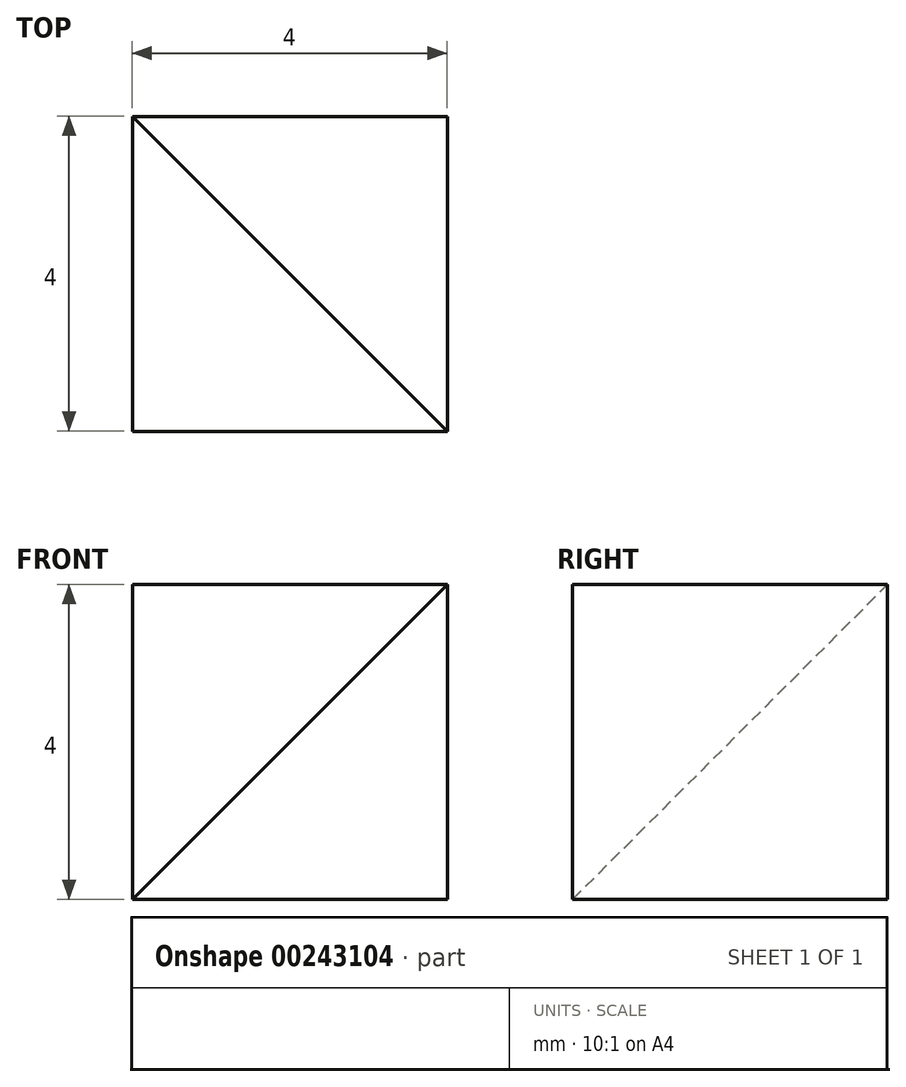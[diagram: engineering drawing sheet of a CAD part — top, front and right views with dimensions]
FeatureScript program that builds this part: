
annotation { "Feature Type Name" : "Feature", "Feature Type Description" : "" }
export const myFeature = defineFeature(function(context is Context, id is Id, definition is map)
    precondition{}
    {
        {
            var Q0;
            Q0=qCreatedBy(makeId("Top.planeOp"),FACE);
            var sketch = newSketch(context, id + "F0", { "sketchPlane" : qUnion([Q0])});
            skLineSegment(sketch, "E0.bottom", {"start": v(20.07, 23.16) * mm, "end": v(24.07, 23.16) * mm});
            skLineSegment(sketch, "E0.top", {"start": v(20.07, 19.16) * mm, "end": v(24.07, 19.16) * mm});
            skLineSegment(sketch, "E0.left", {"start": v(20.07, 23.16) * mm, "end": v(20.07, 19.16) * mm});
            skLineSegment(sketch, "E0.right", {"start": v(24.07, 23.16) * mm, "end": v(24.07, 19.16) * mm});
            skSolve(sketch);
        }
        {
            var Q0;
            Q0=makeQuery(id+"F0.imprint","IMPRINT",FACE,{"disambiguationData":[TD([[makeQuery(id+"F0.imprint","IMPRINT",EDGE,{"derivedFrom":sQuery(id+"F0.wireOp",EDGE,"E0.bottom")}),-1.0]])]});
            extrude(context, id + "F1", {"entities" : qUnion([Q0]), "depth" : 4 * mm});
        }
        {
            var Q0;
            Q0=makeQuery(id+"F1.opExtrude","CAP_VERTEX",VERTEX,{"disambiguationData":[OSD([sQuery(id+"F0.wireOp",EDGE,"E0.bottom"),sQuery(id+"F0.wireOp",EDGE,"E0.left")])],"isStart":false});
            var Q1;
            Q1=makeQuery(id+"F1.opExtrude","CAP_VERTEX",VERTEX,{"disambiguationData":[OSD([sQuery(id+"F0.wireOp",EDGE,"E0.top"),sQuery(id+"F0.wireOp",EDGE,"E0.right")])],"isStart":false});
            var Q2;
            Q2=makeQuery(id+"F1.opExtrude","CAP_VERTEX",VERTEX,{"disambiguationData":[OSD([sQuery(id+"F0.wireOp",EDGE,"E0.top"),sQuery(id+"F0.wireOp",EDGE,"E0.left")])],"isStart":true});
            cPlane(context, id + "F2", {"entities" : qUnion([Q0, Q1, Q2]), "cplaneType" : CPlaneType.THREE_POINT, "offset" : 25 * mm, "width" : 150 * mm, "height" : 150 * mm});
        }
        {
            var Q0;
            Q0=qCreatedBy(id+"F2.planeOp",FACE);
            var sketch = newSketch(context, id + "F3", { "sketchPlane" : qUnion([Q0])});
            skPoint(sketch, "E1.0", {"position": v(8.57, 19.2) * mm});
            skPoint(sketch, "E2.0", {"position": v(13.47, 16.37) * mm});
            skPoint(sketch, "E3.0", {"position": v(8.57, 13.55) * mm});
            skLineSegment(sketch, "E4", {"start": v(8.57, 19.2) * mm, "end": v(13.47, 16.37) * mm});
            skLineSegment(sketch, "E5", {"start": v(13.47, 16.37) * mm, "end": v(8.57, 13.55) * mm});
            skLineSegment(sketch, "E6", {"start": v(8.57, 13.55) * mm, "end": v(8.57, 19.2) * mm});
            skSolve(sketch);
        }
        {
            var Q0;
            Q0 = qSketchRegion(id + "F3", true);
            extrude(context, id + "F4", {"entities" : qUnion([Q0]), "operationType" : NewBodyOperationType.REMOVE, "depth" : 25 * mm});
        }
        {
            var Q0;
            Q0=makeQuery(id+"F1.opExtrude","CAP_VERTEX",VERTEX,{"disambiguationData":[OSD([sQuery(id+"F0.wireOp",EDGE,"E0.bottom"),sQuery(id+"F0.wireOp",EDGE,"E0.right")])],"isStart":true});
            var Q1;
            Q1=makeQuery(id+"F4.boolean.opBoolean","MERGE",VERTEX,{"derivedFrom":[makeQuery(id+"F1.opExtrude","CAP_VERTEX",VERTEX,{"disambiguationData":[OSD([sQuery(id+"F0.wireOp",EDGE,"E0.top"),sQuery(id+"F0.wireOp",EDGE,"E0.right")])],"isStart":false}),makeQuery(id+"F4.opExtrude","CAP_VERTEX",VERTEX,{"disambiguationData":[OSD([sQuery(id+"F3.wireOp",EDGE,"E4"),sQuery(id+"F3.wireOp",EDGE,"E5")])],"isStart":true})]});
            var Q2;
            Q2=makeQuery(id+"F4.boolean.opBoolean","MERGE",VERTEX,{"derivedFrom":[makeQuery(id+"F1.opExtrude","CAP_VERTEX",VERTEX,{"disambiguationData":[OSD([sQuery(id+"F0.wireOp",EDGE,"E0.bottom"),sQuery(id+"F0.wireOp",EDGE,"E0.left")])],"isStart":false}),makeQuery(id+"F4.opExtrude","CAP_VERTEX",VERTEX,{"disambiguationData":[OSD([sQuery(id+"F3.wireOp",EDGE,"E4"),sQuery(id+"F3.wireOp",EDGE,"E6")])],"isStart":true})]});
            cPlane(context, id + "F5", {"entities" : qUnion([Q0, Q1, Q2]), "cplaneType" : CPlaneType.THREE_POINT, "offset" : 25 * mm, "width" : 150 * mm, "height" : 150 * mm});
        }
        {
            var Q0;
            Q0=qCreatedBy(id+"F5.planeOp",FACE);
            var sketch = newSketch(context, id + "F6", { "sketchPlane" : qUnion([Q0])});
            skPoint(sketch, "E7.0", {"position": v(9.08, -11.37) * mm});
            skPoint(sketch, "E8.0", {"position": v(9.08, -17.02) * mm});
            skPoint(sketch, "E9.0", {"position": v(4.18, -14.2) * mm});
            skLineSegment(sketch, "E10", {"start": v(9.08, -11.37) * mm, "end": v(4.18, -14.2) * mm});
            skLineSegment(sketch, "E11", {"start": v(4.18, -14.2) * mm, "end": v(9.08, -17.02) * mm});
            skLineSegment(sketch, "E12", {"start": v(9.08, -17.02) * mm, "end": v(9.08, -11.37) * mm});
            skSolve(sketch);
        }
        {
            var Q0;
            Q0 = qSketchRegion(id + "F6", true);
            extrude(context, id + "F7", {"entities" : qUnion([Q0]), "operationType" : NewBodyOperationType.REMOVE, "depth" : 25 * mm});
        }
    });
